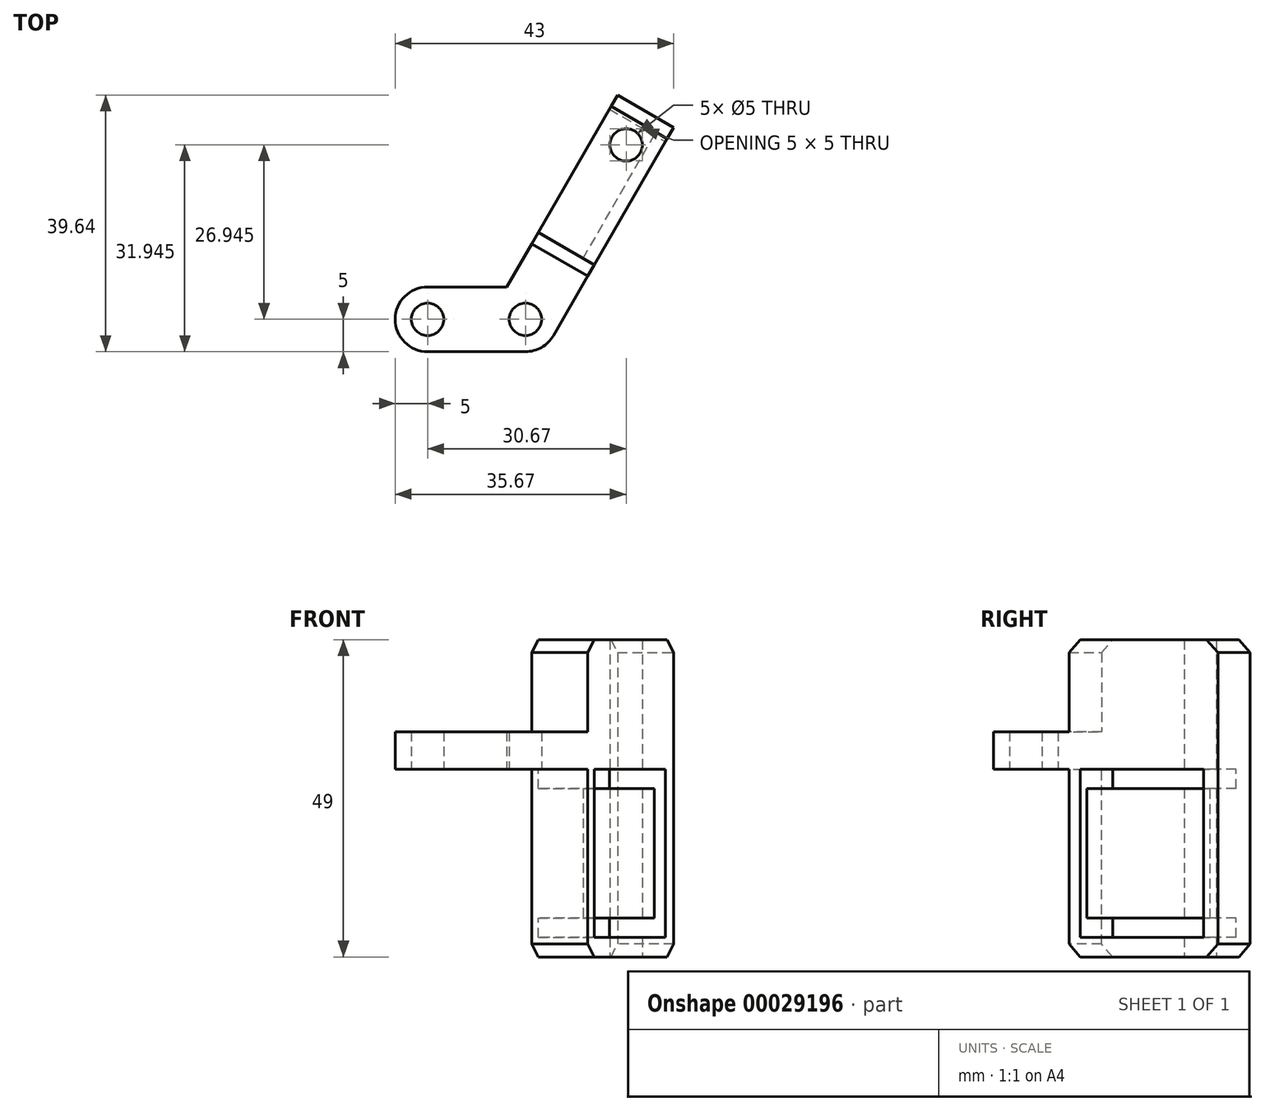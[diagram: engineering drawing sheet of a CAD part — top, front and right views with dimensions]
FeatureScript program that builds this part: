
annotation { "Feature Type Name" : "Feature", "Feature Type Description" : "" }
export const myFeature = defineFeature(function(context is Context, id is Id, definition is map)
    precondition{}
    {
        {
            var Q0;
            Q0=qCreatedBy(makeId("Top.planeOp"),FACE);
            var sketch = newSketch(context, id + "F0", { "sketchPlane" : qUnion([Q0])});
            skLineSegment(sketch, "E0", {"start": v(5, 0) * mm, "end": v(20.11, 0) * mm});
            skLineSegment(sketch, "E1", {"start": v(24.44, 2.5) * mm, "end": v(43, 34.64) * mm});
            skLineSegment(sketch, "E2", {"start": v(43, 34.64) * mm, "end": v(34.34, 39.64) * mm});
            skLineSegment(sketch, "E3", {"start": v(0, 5) * mm, "end": v(0, 5) * mm});
            skLineSegment(sketch, "E4", {"start": v(5, 10) * mm, "end": v(17.23, 10) * mm});
            skLineSegment(sketch, "E5", {"start": v(17.23, 10) * mm, "end": v(34.34, 39.64) * mm});
            skCircle(sketch, "E6", {"center": v(5, 5) * mm, "radius": 2.5 * mm});
            skCircle(sketch, "E7", {"center": v(35.67, 31.94) * mm, "radius": 2.5 * mm});
            skPoint(sketch, "E8.visualSharp", {"position": v(0, 10) * mm});
            skArc(sketch, "E8.filletArc", {"start": v(5, 10) * mm, "mid": v(1.46, 8.54) * mm, "end": v(0, 5) * mm});
            skPoint(sketch, "E9.visualSharp", {"position": v(0, 0) * mm});
            skArc(sketch, "E9.filletArc", {"start": v(0, 5) * mm, "mid": v(1.46, 1.46) * mm, "end": v(5, 0) * mm});
            skPoint(sketch, "E10.visualSharp", {"position": v(23, 0) * mm});
            skArc(sketch, "E10.filletArc", {"start": v(20.11, 0) * mm, "mid": v(22.61, 0.67) * mm, "end": v(24.44, 2.5) * mm});
            skCircle(sketch, "E11", {"center": v(20.11, 5) * mm, "radius": 2.5 * mm});
            skLineSegment(sketch, "E12", {"start": v(21.08, 16.67) * mm, "end": v(29.74, 11.67) * mm});
            skSolve(sketch);
        }
        {
            var Q0;
            Q0=makeQuery(id+"F0.imprint","IMPRINT",FACE,{"disambiguationData":[TD([[makeQuery(id+"F0.imprint","IMPRINT",EDGE,{"derivedFrom":sQuery(id+"F0.wireOp",EDGE,"E0")}),1.0]])]});
            extrude(context, id + "F1", {"entities" : qUnion([Q0]), "depth" : 5.8 * mm});
        }
        {
            var Q0;
            {var subQ2=sQuery(id+"F0.wireOp",EDGE,"E2");Q0=makeQuery(id+"F0.imprint","IMPRINT",FACE,{"disambiguationData":[TD([[makeQuery(id+"F0.imprint","IMPRINT",EDGE,{"derivedFrom":subQ2}),1.0]])]});}
            extrude(context, id + "F2", {"entities" : qUnion([Q0]), "operationType" : NewBodyOperationType.ADD, "depth" : 20 * mm});
        }
        {
            var Q0;
            {var subQ2=sQuery(id+"F0.wireOp",EDGE,"E2");Q0=makeQuery(id+"F0.imprint","IMPRINT",FACE,{"disambiguationData":[TD([[makeQuery(id+"F0.imprint","IMPRINT",EDGE,{"derivedFrom":subQ2}),1.0]])]});}
            extrude(context, id + "F3", {"entities" : qUnion([Q0]), "operationType" : NewBodyOperationType.ADD, "oppositeDirection" : true, "depth" : 29 * mm});
        }
        {
            var Q0;
            Q0=makeQuery(id+"F3.opExtrude","CAP_EDGE",EDGE,{"disambiguationData":[OSD([sQuery(id+"F0.wireOp",EDGE,"E2")])],"isStart":false});
            var Q1;
            Q1=makeQuery(id+"F3.opExtrude","CAP_EDGE",EDGE,{"disambiguationData":[OSD([sQuery(id+"F0.wireOp",EDGE,"E12")])],"isStart":false});
            var Q2;
            Q2=makeQuery(id+"F2.opExtrude","CAP_EDGE",EDGE,{"disambiguationData":[OSD([sQuery(id+"F0.wireOp",EDGE,"E12")])],"isStart":false});
            var Q3;
            Q3=makeQuery(id+"F2.opExtrude","CAP_EDGE",EDGE,{"disambiguationData":[OSD([sQuery(id+"F0.wireOp",EDGE,"E2")])],"isStart":false});
            chamfer(context, id + "F4", {"entities" : qUnion([Q0, Q1, Q2, Q3]), "width" : 2 * mm, "tangentPropagation" : true});
        }
        {
            var Q0;
            {var subQ0=sQuery(id+"F0.wireOp",EDGE,"E1");Q0=makeQuery(id+"F3.boolean.opBoolean","MERGE",FACE,{"derivedFrom":[makeQuery(id+"F2.boolean.opBoolean","MERGE",FACE,{"derivedFrom":[makeQuery(id+"F1.opExtrude","SWEPT_FACE",FACE,{"disambiguationData":[OSD([subQ0])]}),makeQuery(id+"F2.opExtrude","SWEPT_FACE",FACE,{"disambiguationData":[OSD([subQ0])]})]}),makeQuery(id+"F3.opExtrude","SWEPT_FACE",FACE,{"disambiguationData":[OSD([subQ0])]})]});}
            var sketch = newSketch(context, id + "F5", { "sketchPlane" : qUnion([Q0])});
            skLineSegment(sketch, "E13.bottom", {"start": v(26.97, 0) * mm, "end": v(48.97, 0) * mm});
            skLineSegment(sketch, "E13.top", {"start": v(26.97, -3) * mm, "end": v(48.97, -3) * mm});
            skLineSegment(sketch, "E13.left", {"start": v(26.97, 0) * mm, "end": v(26.97, -3) * mm});
            skLineSegment(sketch, "E13.right", {"start": v(48.97, 0) * mm, "end": v(48.97, -3) * mm});
            skPoint(sketch, "E14.firstSnap0", {"position": v(26.97, -1.5) * mm});
            skLineSegment(sketch, "E14.bottom", {"start": v(26.97, -23) * mm, "end": v(48.97, -23) * mm});
            skLineSegment(sketch, "E14.top", {"start": v(26.97, -26) * mm, "end": v(48.97, -26) * mm});
            skLineSegment(sketch, "E14.left", {"start": v(26.97, -23) * mm, "end": v(26.97, -26) * mm});
            skLineSegment(sketch, "E14.right", {"start": v(48.97, -23) * mm, "end": v(48.97, -26) * mm});
            skLineSegment(sketch, "E15", {"start": v(26.97, -3) * mm, "end": v(26.97, -23) * mm});
            skLineSegment(sketch, "E16", {"start": v(48.97, -23) * mm, "end": v(48.97, -3) * mm});
            skSolve(sketch);
        }
        {
            var Q0;
            Q0=makeQuery(id+"F5.imprint","IMPRINT",FACE,{"disambiguationData":[TD([[makeQuery(id+"F5.imprint","IMPRINT",EDGE,{"derivedFrom":sQuery(id+"F5.wireOp",EDGE,"E13.top")}),-1.0]])]});
            extrude(context, id + "F6", {"entities" : qUnion([Q0]), "operationType" : NewBodyOperationType.REMOVE, "oppositeDirection" : true, "depth" : 2 * mm});
        }
        {
            var Q0;
            Q0=makeQuery(id+"F5.imprint","IMPRINT",FACE,{"disambiguationData":[TD([[makeQuery(id+"F5.imprint","IMPRINT",EDGE,{"derivedFrom":sQuery(id+"F5.wireOp",EDGE,"E14.bottom")}),-1.0]])]});
            var Q1;
            Q1=makeQuery(id+"F5.imprint","IMPRINT",FACE,{"disambiguationData":[TD([[makeQuery(id+"F5.imprint","IMPRINT",EDGE,{"derivedFrom":sQuery(id+"F5.wireOp",EDGE,"E13.bottom")}),-1.0]])]});
            extrude(context, id + "F7", {"entities" : qUnion([Q0, Q1]), "operationType" : NewBodyOperationType.REMOVE, "endBound" : BoundingType.THROUGH_ALL, "oppositeDirection" : true, "depth" : 25 * mm});
        }
    });
